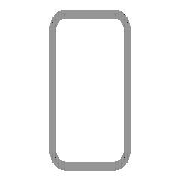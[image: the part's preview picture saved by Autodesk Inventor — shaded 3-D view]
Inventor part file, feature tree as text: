
AUTODESK INVENTOR PART (.ipt)
format: ipt  version: 2025 (Build 290162010, 162A)  size: 133,120 bytes
history: native  units: mm (DEFAULTED — no unit token found)
features: other x4, sketch x1, plane x1
ambient origin geometry x8: Origin, YZ Plane, XZ Plane, XY Plane, X Axis, Y Axis, Z Axis, Center Point
bodies: Solid1 (feature_tree), Body (feature_tree)
feature tree (6):
  parser-record x1  (decoder bookkeeping rows leaked as tree rows — omitted from the tree; the rows remain in map.json)
  other  "Driven Length"
  other  "Start Plane"
  other  "End Plane"
  sketch  "Sketch3"  dims[d3=1500.0mm d4=0.0mm d7=6.0mm d9=40.0mm d11=60.0mm d12=3.0mm d13=-0.0mm d14=1500.0mm d15=20.0mm d16=30.0mm d17=90.0deg d18=1500.0mm]
  plane  "Work Plane3"
